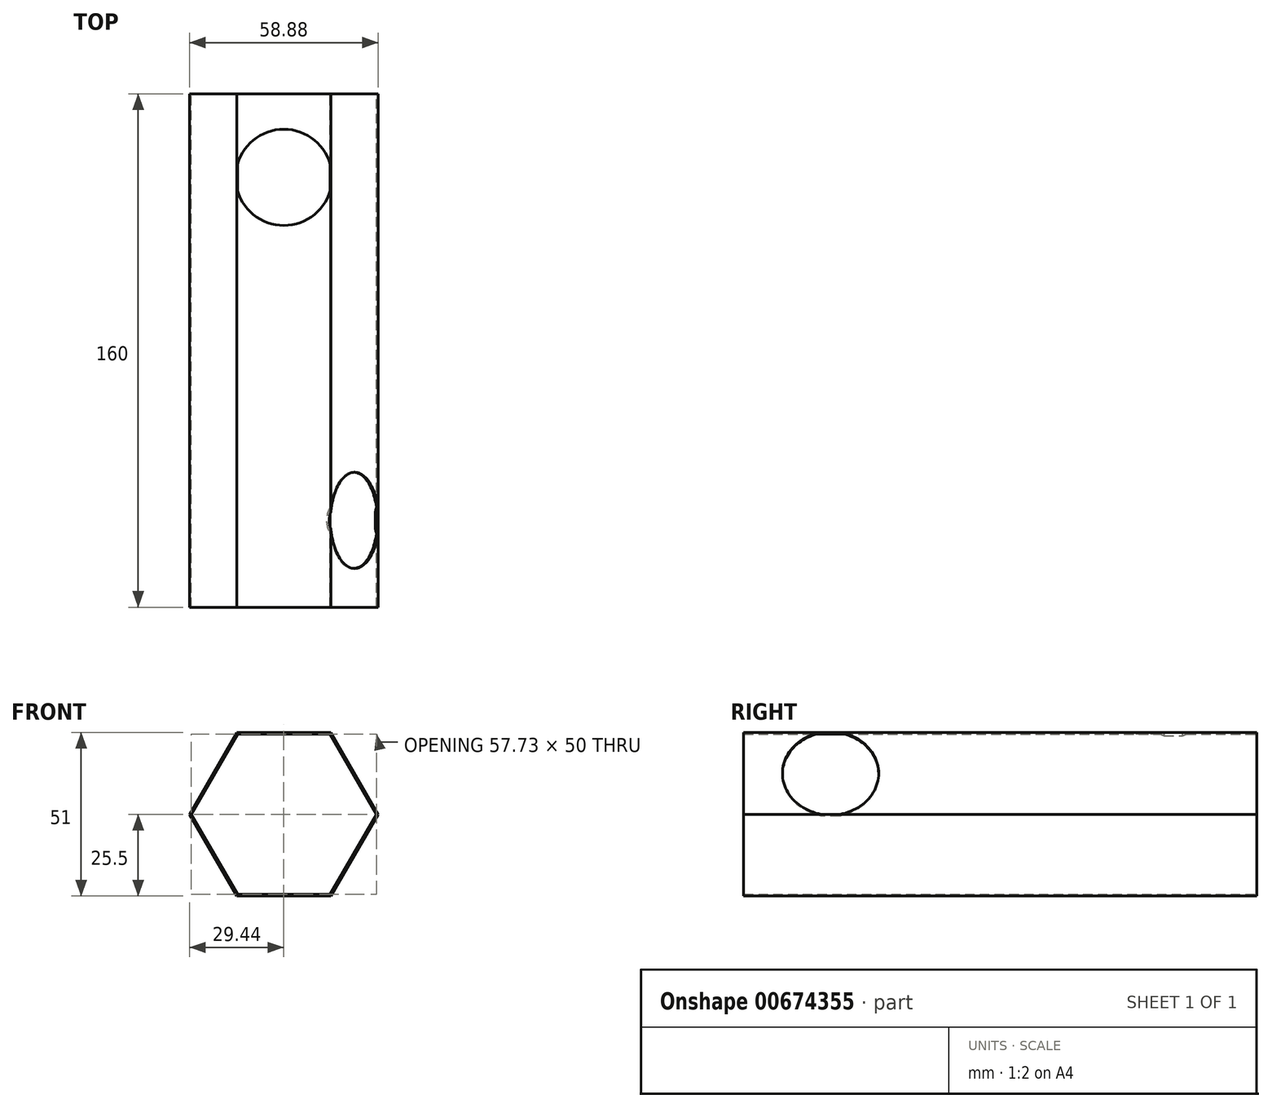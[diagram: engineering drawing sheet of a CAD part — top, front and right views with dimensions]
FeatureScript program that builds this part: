
annotation { "Feature Type Name" : "Feature", "Feature Type Description" : "" }
export const myFeature = defineFeature(function(context is Context, id is Id, definition is map)
    precondition{}
    {
        {
            var Q0;
            Q0=qCreatedBy(makeId("Front.planeOp"),FACE);
            var sketch = newSketch(context, id + "F0", { "sketchPlane" : qUnion([Q0])});
            skCircle(sketch, "E0.cCircle", {"center": v(0, 0) * mm, "radius": 25.5 * mm, "construction": true});
            skLineSegment(sketch, "E0.0", {"start": v(-14.72, 25.5) * mm, "end": v(14.72, 25.5) * mm});
            skLineSegment(sketch, "E0.1", {"start": v(14.72, 25.5) * mm, "end": v(29.44, 0) * mm});
            skLineSegment(sketch, "E0.2", {"start": v(29.44, 0) * mm, "end": v(14.72, -25.5) * mm});
            skLineSegment(sketch, "E0.3", {"start": v(14.72, -25.5) * mm, "end": v(-14.72, -25.5) * mm});
            skLineSegment(sketch, "E0.4", {"start": v(-14.72, -25.5) * mm, "end": v(-29.44, 0) * mm});
            skLineSegment(sketch, "E0.5", {"start": v(-29.44, 0) * mm, "end": v(-14.72, 25.5) * mm});
            skPoint(sketch, "E0.0.midPoint", {"position": v(0, 25.5) * mm});
            skCircle(sketch, "E1.cCircle", {"center": v(0, 0) * mm, "radius": 25 * mm, "construction": true});
            skLineSegment(sketch, "E1.0", {"start": v(-14.43, 25) * mm, "end": v(14.43, 25) * mm});
            skLineSegment(sketch, "E1.1", {"start": v(14.43, 25) * mm, "end": v(28.87, 0) * mm});
            skLineSegment(sketch, "E1.2", {"start": v(28.87, 0) * mm, "end": v(14.43, -25) * mm});
            skLineSegment(sketch, "E1.3", {"start": v(14.43, -25) * mm, "end": v(-14.43, -25) * mm});
            skLineSegment(sketch, "E1.4", {"start": v(-14.43, -25) * mm, "end": v(-28.87, 0) * mm});
            skLineSegment(sketch, "E1.5", {"start": v(-28.87, 0) * mm, "end": v(-14.43, 25) * mm});
            skPoint(sketch, "E1.0.midPoint", {"position": v(0, 25) * mm});
            skLineSegment(sketch, "E2.bottom", {"start": v(-14.43, -25) * mm, "end": v(14.72, -25) * mm});
            skLineSegment(sketch, "E3.bottom", {"start": v(-12.72, -25) * mm, "end": v(12.72, -25) * mm});
            skSolve(sketch);
        }
        {
            var Q0;
            Q0=makeQuery(id+"F0.imprint","IMPRINT",FACE,{"disambiguationData":[TD([[makeQuery(id+"F0.imprint","IMPRINT",EDGE,{"derivedFrom":sQuery(id+"F0.wireOp",EDGE,"E0.0")}),-1.0]])]});
            extrude(context, id + "F1", {"entities" : qUnion([Q0]), "depth" : 160 * mm, "offsetDistance" : 25 * mm});
        }
        {
            var Q0;
            {var subQ0=sQuery(id+"F0.wireOp",EDGE,"E2.top");Q0=makeQuery(id+"F0.imprint","IMPRINT",FACE,{"disambiguationData":[TD([[makeQuery(id+"F0.imprint","IMPRINT",EDGE,{"derivedFrom":subQ0}),-1.0]])]});}
            var Q1;
            {var subQ0=sQuery(id+"F0.wireOp",EDGE,"E2.bottom");var subQ1=sQuery(id+"F0.wireOp",EDGE,"E1.2");var subQ2=makeQuery(id+"F0.imprint","INTERSECT",VERTEX,{"derivedFrom":[subQ1,subQ0]});Q1=makeQuery(id+"F0.imprint","IMPRINT",FACE,{"disambiguationData":[TD([[makeQuery(id+"F0.imprint","IMPRINT",EDGE,{"disambiguationData":[TD([[subQ2,1.0]])],"derivedFrom":subQ1}),1.0]])]});}
            extrude(context, id + "F2", {"entities" : qUnion([Q0, Q1]), "operationType" : NewBodyOperationType.ADD, "depth" : 140 * mm, "offsetDistance" : 25 * mm});
        }
        {
            var Q0;
            Q0=makeQuery(id+"F1.opExtrude","SWEPT_FACE",FACE,{"disambiguationData":[OSD([sQuery(id+"F0.wireOp",EDGE,"E0.1")])]});
            var sketch = newSketch(context, id + "F3", { "sketchPlane" : qUnion([Q0])});
            skCircle(sketch, "E4", {"center": v(-132.91, 0) * mm, "radius": 15 * mm});
            skSolve(sketch);
        }
        {
            var Q0;
            {var subQ0=sQuery(id+"F3.wireOp",EDGE,"E4");var subQ1=makeQuery(id+"F1.opExtrude","SWEPT_EDGE",EDGE,{"disambiguationData":[OSD([sQuery(id+"F0.wireOp",EDGE,"E0.0"),sQuery(id+"F0.wireOp",EDGE,"E0.1")])]});var subQ2=makeQuery(id+"F3.imprint","INTERSECT",VERTEX,{"disambiguationData":[OD(0.0)],"derivedFrom":[subQ1,subQ0]});Q0=makeQuery(id+"F3.imprint","IMPRINT",FACE,{"disambiguationData":[TD([[makeQuery(id+"F3.imprint","IMPRINT",EDGE,{"disambiguationData":[TD([[subQ2,1.0]])],"derivedFrom":subQ0}),1.0]])]});}
            var Q1;
            {var subQ0=sQuery(id+"F3.wireOp",EDGE,"E4");var subQ1=makeQuery(id+"F1.opExtrude","SWEPT_EDGE",EDGE,{"disambiguationData":[OSD([sQuery(id+"F0.wireOp",EDGE,"E0.1"),sQuery(id+"F0.wireOp",EDGE,"E0.2")])]});var subQ2=makeQuery(id+"F3.imprint","INTERSECT",VERTEX,{"disambiguationData":[OD(0.0)],"derivedFrom":[subQ1,subQ0]});Q1=makeQuery(id+"F3.imprint","IMPRINT",FACE,{"disambiguationData":[TD([[makeQuery(id+"F3.imprint","IMPRINT",EDGE,{"disambiguationData":[TD([[subQ2,-1.0]])],"derivedFrom":subQ0}),1.0]])]});}
            var Q2;
            {var subQ0=sQuery(id+"F3.wireOp",EDGE,"E4");var subQ1=sQuery(id+"F0.wireOp",EDGE,"E0.1");var subQ2=makeQuery(id+"F1.opExtrude","SWEPT_EDGE",EDGE,{"disambiguationData":[OSD([sQuery(id+"F0.wireOp",EDGE,"E0.0"),subQ1])]});var subQ3=makeQuery(id+"F3.imprint","INTERSECT",VERTEX,{"disambiguationData":[OD(0.0)],"derivedFrom":[subQ2,subQ0]});Q2=makeQuery(id+"F3.imprint","IMPRINT",FACE,{"disambiguationData":[TD([[makeQuery(id+"F3.imprint","IMPRINT",EDGE,{"disambiguationData":[TD([[subQ3,-1.0]])],"derivedFrom":subQ0}),1.0]])]});}
            extrude(context, id + "F4", {"entities" : qUnion([Q0, Q1, Q2]), "operationType" : NewBodyOperationType.REMOVE, "endBound" : BoundingType.UP_TO_NEXT, "oppositeDirection" : true, "depth" : 25 * mm, "offsetDistance" : 25 * mm});
        }
        {
            var Q0;
            Q0=makeQuery(id+"F1.opExtrude","SWEPT_FACE",FACE,{"disambiguationData":[OSD([sQuery(id+"F0.wireOp",EDGE,"E0.0")])]});
            var sketch = newSketch(context, id + "F5", { "sketchPlane" : qUnion([Q0])});
            skCircle(sketch, "E5", {"center": v(0, -26.03) * mm, "radius": 15 * mm});
            skSolve(sketch);
        }
        {
            var Q0;
            {var subQ5=sQuery(id+"F0.wireOp",EDGE,"E0.0");var subQ7=makeQuery(id+"F1.opExtrude","SWEPT_FACE",FACE,{"disambiguationData":[OSD([subQ5])]});var subQ8=makeQuery(id+"F3Vo0p6nTAKC7f0_1.opExtrude","SWEPT_FACE",FACE,{"disambiguationData":[OSD([sQuery(id+"FlhWOkEc3YPRbqO_1.wireOp",EDGE,"bpZJyePA-Y9T3-hnbQ-g8yD-iRAMQkEPoKtL")])]});var subQ10=makeQuery(id+"F3Vo0p6nTAKC7f0_1.boolean.opBoolean","INTERSECT",EDGE,{"derivedFrom":[subQ7,subQ8]});var subQ12=sQuery(id+"F5.wireOp",EDGE,"E5");var subQ13=makeQuery(id+"F5.imprint","INTERSECT",VERTEX,{"derivedFrom":[subQ10,subQ12]});Q0=makeQuery(id+"F5.imprint","IMPRINT",FACE,{"disambiguationData":[TD([[makeQuery(id+"F5.imprint","IMPRINT",EDGE,{"disambiguationData":[TD([[subQ13,-1.0]])],"derivedFrom":subQ12}),1.0]])]});}
            var Q1;
            Q1=makeQuery(id+"F1.opExtrude","SWEPT_FACE",FACE,{"disambiguationData":[OSD([sQuery(id+"F0.wireOp",EDGE,"E2.bottom"),sQuery(id+"F0.wireOp",EDGE,"E3.bottom")])]});
            extrude(context, id + "F6", {"entities" : qUnion([Q0]), "operationType" : NewBodyOperationType.REMOVE, "oppositeDirection" : true, "depth" : 5 * mm, "endBoundEntityFace" : qUnion([Q1]), "offsetDistance" : 25 * mm});
        }
    });
